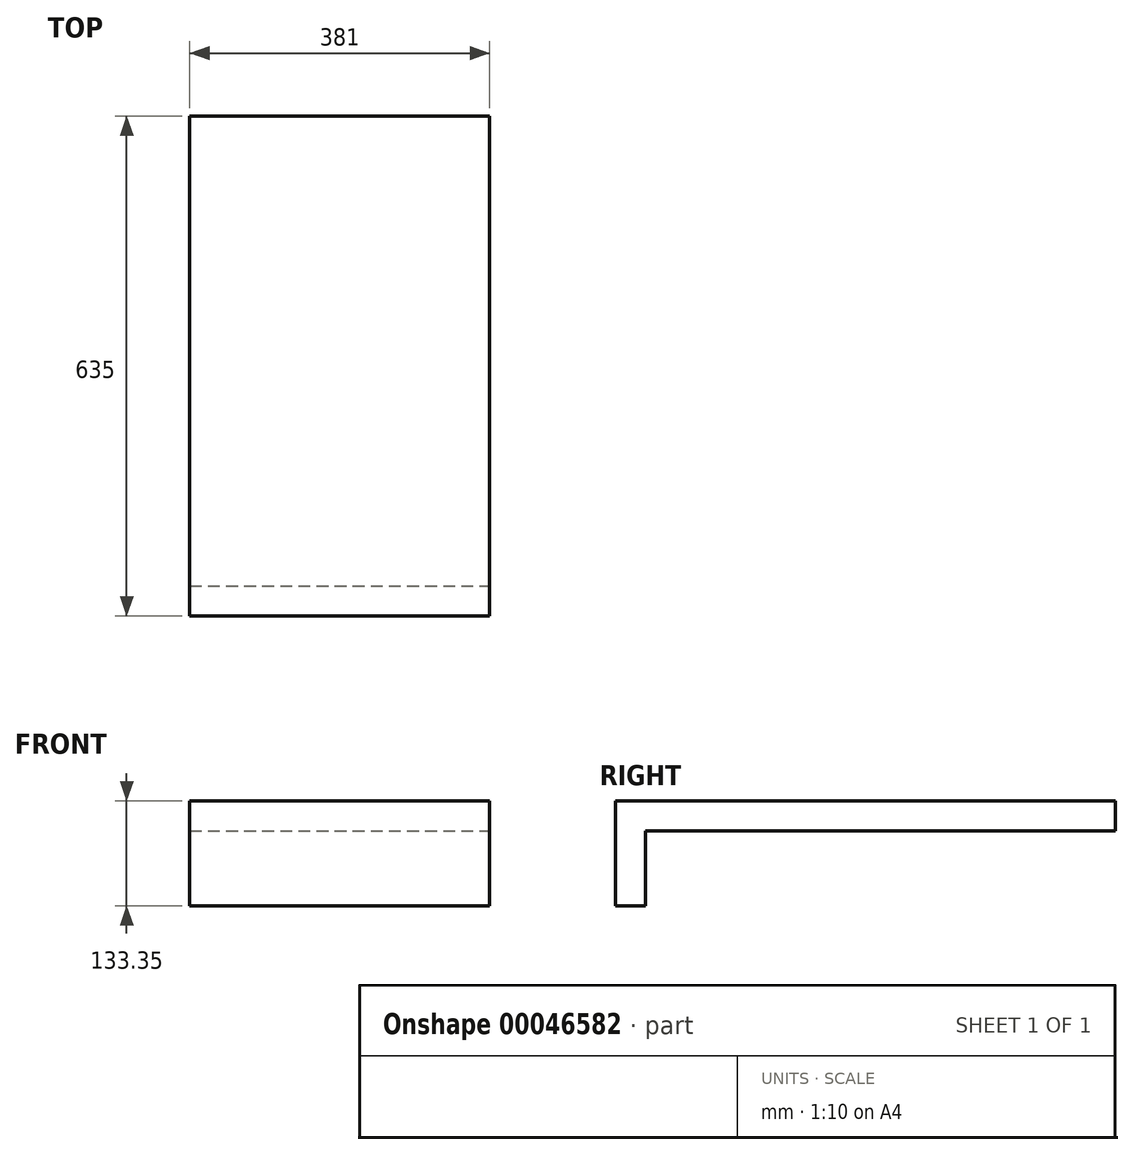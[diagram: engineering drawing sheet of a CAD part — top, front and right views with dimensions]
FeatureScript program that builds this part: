
annotation { "Feature Type Name" : "Feature", "Feature Type Description" : "" }
export const myFeature = defineFeature(function(context is Context, id is Id, definition is map)
    precondition{}
    {
        {
            var Q0;
            Q0=qCreatedBy(makeId("Top.planeOp"),FACE);
            var sketch = newSketch(context, id + "F0", { "sketchPlane" : qUnion([Q0])});
            skLineSegment(sketch, "E0.rect.bottom", {"start": v(190.5, 317.5) * mm, "end": v(-190.5, 317.5) * mm});
            skLineSegment(sketch, "E0.rect.top", {"start": v(190.5, -317.5) * mm, "end": v(-190.5, -317.5) * mm});
            skLineSegment(sketch, "E0.rect.left", {"start": v(190.5, 317.5) * mm, "end": v(190.5, -317.5) * mm});
            skLineSegment(sketch, "E0.rect.right", {"start": v(-190.5, 317.5) * mm, "end": v(-190.5, -317.5) * mm});
            skPoint(sketch, "E0.rect.middle", {"position": v(0, 0) * mm});
            skSolve(sketch);
        }
        {
            var Q0;
            Q0=makeQuery(id+"F0.imprint","IMPRINT",FACE,{"disambiguationData":[TD([[makeQuery(id+"F0.imprint","IMPRINT",EDGE,{"derivedFrom":sQuery(id+"F0.wireOp",EDGE,"E0.rect.bottom")}),1.0]])]});
            extrude(context, id + "F1", {"entities" : qUnion([Q0]), "depth" : 38.1 * mm});
        }
        {
            var Q0;
            Q0=makeQuery(id+"F1.opExtrude","CAP_FACE",FACE,{"disambiguationData":[OSD([sQuery(id+"F0.wireOp",EDGE,"E0.rect.bottom"),sQuery(id+"F0.wireOp",EDGE,"E0.rect.top"),sQuery(id+"F0.wireOp",EDGE,"E0.rect.left"),sQuery(id+"F0.wireOp",EDGE,"E0.rect.right")])],"isStart":true});
            var sketch = newSketch(context, id + "F2", { "sketchPlane" : qUnion([Q0])});
            skLineSegment(sketch, "E1.bottom", {"start": v(-190.5, 317.5) * mm, "end": v(190.5, 317.5) * mm});
            skLineSegment(sketch, "E1.top", {"start": v(-190.5, 279.4) * mm, "end": v(190.5, 279.4) * mm});
            skLineSegment(sketch, "E1.left", {"start": v(-190.5, 317.5) * mm, "end": v(-190.5, 279.4) * mm});
            skLineSegment(sketch, "E1.right", {"start": v(190.5, 317.5) * mm, "end": v(190.5, 279.4) * mm});
            skSolve(sketch);
        }
        {
            var Q0;
            Q0 = qSketchRegion(id + "F2", true);
            extrude(context, id + "F3", {"entities" : qUnion([Q0]), "operationType" : NewBodyOperationType.ADD, "depth" : 95.25 * mm});
        }
    });
